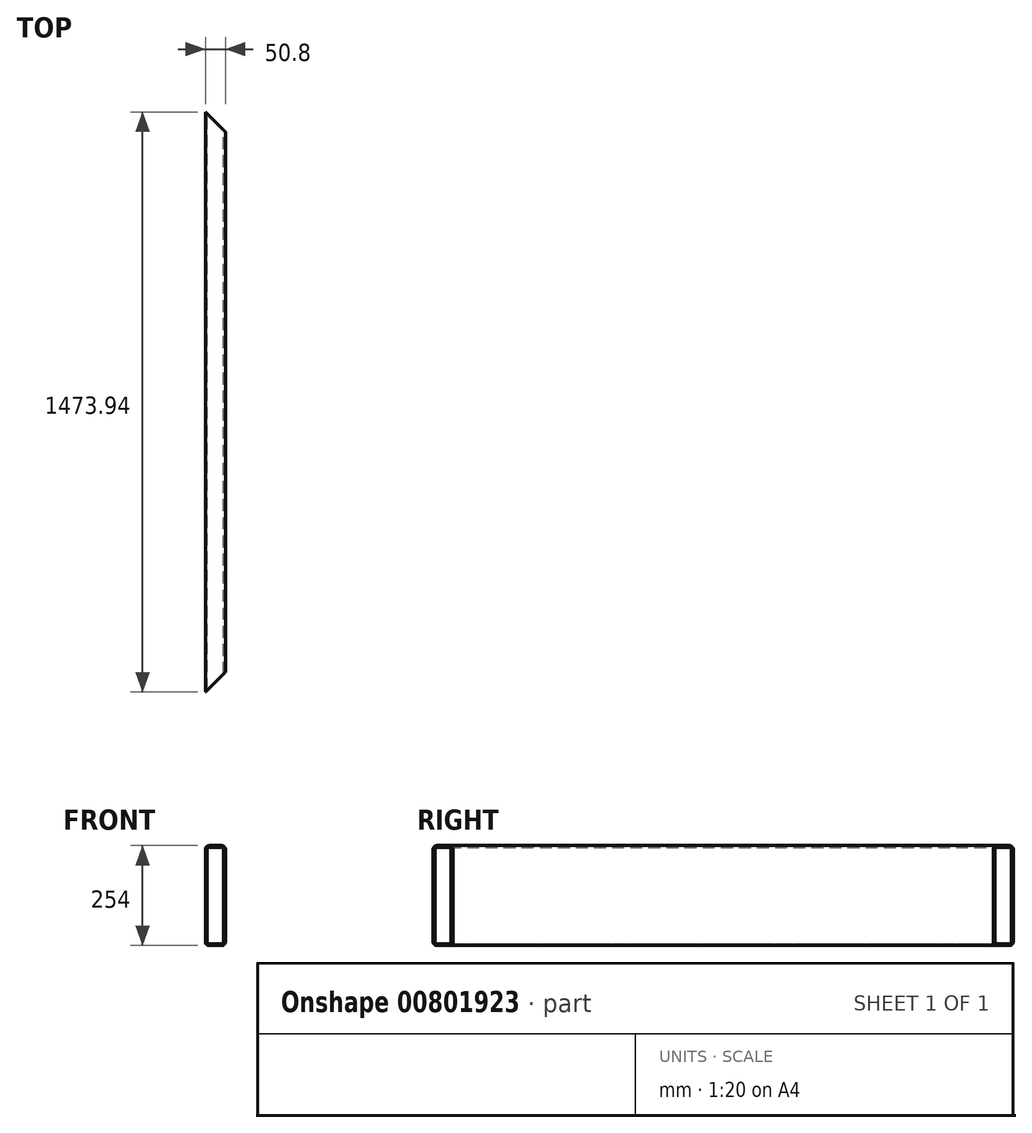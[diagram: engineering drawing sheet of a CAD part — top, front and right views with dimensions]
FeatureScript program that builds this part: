
annotation { "Feature Type Name" : "Feature", "Feature Type Description" : "" }
export const myFeature = defineFeature(function(context is Context, id is Id, definition is map)
    precondition{}
    {
        {
            var Q0;
            Q0=qCreatedBy(makeId("Front.planeOp"),FACE);
            var sketch = newSketch(context, id + "F0", { "sketchPlane" : qUnion([Q0])});
            skLineSegment(sketch, "E0.bottom", {"start": v(-9.52, 0) * mm, "end": v(-41.28, 0) * mm});
            skLineSegment(sketch, "E0.top", {"start": v(-9.53, 254) * mm, "end": v(-41.28, 254) * mm});
            skLineSegment(sketch, "E0.left", {"start": v(0, 9.53) * mm, "end": v(0, 244.47) * mm});
            skLineSegment(sketch, "E0.right", {"start": v(-50.8, 9.52) * mm, "end": v(-50.8, 244.47) * mm});
            skLineSegment(sketch, "E1.bottom", {"start": v(-41.3, 249.25) * mm, "end": v(-9.5, 249.25) * mm});
            skLineSegment(sketch, "E1.top", {"start": v(-41.3, 4.75) * mm, "end": v(-9.5, 4.75) * mm});
            skLineSegment(sketch, "E1.left", {"start": v(-46.05, 244.5) * mm, "end": v(-46.05, 9.5) * mm});
            skLineSegment(sketch, "E1.right", {"start": v(-4.75, 244.5) * mm, "end": v(-4.75, 9.5) * mm});
            skPoint(sketch, "E2.visualSharp", {"position": v(-46.05, 249.25) * mm});
            skArc(sketch, "E2.filletArc", {"start": v(-41.3, 249.25) * mm, "mid": v(-44.66, 247.86) * mm, "end": v(-46.05, 244.5) * mm});
            skPoint(sketch, "E3.visualSharp", {"position": v(-4.75, 249.25) * mm});
            skArc(sketch, "E3.filletArc", {"start": v(-4.75, 244.5) * mm, "mid": v(-6.14, 247.86) * mm, "end": v(-9.5, 249.25) * mm});
            skPoint(sketch, "E4.visualSharp", {"position": v(-4.75, 4.75) * mm});
            skArc(sketch, "E4.filletArc", {"start": v(-9.5, 4.75) * mm, "mid": v(-6.14, 6.14) * mm, "end": v(-4.75, 9.5) * mm});
            skPoint(sketch, "E5.visualSharp", {"position": v(-46.05, 4.75) * mm});
            skArc(sketch, "E5.filletArc", {"start": v(-46.05, 9.5) * mm, "mid": v(-44.66, 6.14) * mm, "end": v(-41.3, 4.75) * mm});
            skPoint(sketch, "E6.visualSharp", {"position": v(-50.8, 254) * mm});
            skArc(sketch, "E6.filletArc", {"start": v(-41.28, 254) * mm, "mid": v(-48.01, 251.21) * mm, "end": v(-50.8, 244.47) * mm});
            skPoint(sketch, "E7.visualSharp", {"position": v(0, 254) * mm});
            skArc(sketch, "E7.filletArc", {"start": v(0, 244.47) * mm, "mid": v(-2.79, 251.21) * mm, "end": v(-9.53, 254) * mm});
            skPoint(sketch, "E8.visualSharp", {"position": v(0, 0) * mm});
            skArc(sketch, "E8.filletArc", {"start": v(-9.52, 0) * mm, "mid": v(-2.79, 2.79) * mm, "end": v(0, 9.53) * mm});
            skPoint(sketch, "E9.visualSharp", {"position": v(-50.8, 0) * mm});
            skArc(sketch, "E9.filletArc", {"start": v(-50.8, 9.52) * mm, "mid": v(-48.01, 2.79) * mm, "end": v(-41.28, 0) * mm});
            skSolve(sketch);
        }
        {
            var Q0;
            Q0=qSketchRegion(id+"F0",true);
            extrude(context, id + "F1", {"entities" : qUnion([Q0]), "depth" : 1473.94 * mm});
        }
        {
            var Q0;
            Q0=makeQuery(id+"F1.opExtrude","SWEPT_FACE",FACE,{"disambiguationData":[OSD([sQuery(id+"F0.wireOp",EDGE,"E0.top")])]});
            var sketch = newSketch(context, id + "F2", { "sketchPlane" : qUnion([Q0])});
            skLineSegment(sketch, "E10", {"start": v(-50.8, -1473.94) * mm, "end": v(0, -1423.14) * mm});
            skLineSegment(sketch, "E11", {"start": v(0, -1423.14) * mm, "end": v(0, -1473.94) * mm});
            skLineSegment(sketch, "E12", {"start": v(0, -1473.94) * mm, "end": v(-50.8, -1473.94) * mm});
            skLineSegment(sketch, "E13", {"start": v(-50.8, 0) * mm, "end": v(0, -50.8) * mm});
            skLineSegment(sketch, "E14", {"start": v(0, -50.8) * mm, "end": v(0, 0) * mm});
            skLineSegment(sketch, "E15", {"start": v(0, 0) * mm, "end": v(-50.8, 0) * mm});
            skSolve(sketch);
        }
        {
            var Q0;
            Q0=qSketchRegion(id+"F2",true);
            extrude(context, id + "F3", {"entities" : qUnion([Q0]), "operationType" : NewBodyOperationType.REMOVE, "endBound" : BoundingType.THROUGH_ALL, "oppositeDirection" : true, "depth" : 25.4 * mm});
        }
        {
            var Q0;
            Q0=makeQuery(id+"F1.opExtrude","SWEPT_FACE",FACE,{"disambiguationData":[OSD([sQuery(id+"F0.wireOp",EDGE,"E0.left")])]});
            var sketch = newSketch(context, id + "F4", { "sketchPlane" : qUnion([Q0])});
            skLineSegment(sketch, "E16", {"start": v(-271.44, 383.12) * mm, "end": v(-298.41, 358.62) * mm});
            skLineSegment(sketch, "E17", {"start": v(-262.9, 386.42) * mm, "end": v(-220.1, 386.42) * mm});
            skLineSegment(sketch, "E18", {"start": v(-207.4, 373.72) * mm, "end": v(-207.4, 239) * mm});
            skLineSegment(sketch, "E19", {"start": v(-220.1, 226.3) * mm, "end": v(-289.88, 226.3) * mm});
            skLineSegment(sketch, "E20", {"start": v(-302.58, 239) * mm, "end": v(-302.58, 349.21) * mm});
            skArc(sketch, "E21.filletArc", {"start": v(-262.9, 386.42) * mm, "mid": v(-267.48, 385.56) * mm, "end": v(-271.44, 383.12) * mm});
            skPoint(sketch, "E22.visualSharp", {"position": v(-302.58, 354.84) * mm});
            skArc(sketch, "E22.filletArc", {"start": v(-298.41, 358.62) * mm, "mid": v(-301.49, 354.35) * mm, "end": v(-302.58, 349.21) * mm});
            skPoint(sketch, "E23.visualSharp", {"position": v(-302.58, 226.3) * mm});
            skArc(sketch, "E23.filletArc", {"start": v(-302.58, 239) * mm, "mid": v(-298.86, 230.01) * mm, "end": v(-289.88, 226.3) * mm});
            skPoint(sketch, "E24.visualSharp", {"position": v(-207.4, 226.3) * mm});
            skArc(sketch, "E24.filletArc", {"start": v(-220.1, 226.3) * mm, "mid": v(-211.12, 230.01) * mm, "end": v(-207.4, 239) * mm});
            skPoint(sketch, "E25.visualSharp", {"position": v(-207.4, 386.42) * mm});
            skArc(sketch, "E25.filletArc", {"start": v(-207.4, 373.72) * mm, "mid": v(-211.12, 382.7) * mm, "end": v(-220.1, 386.42) * mm});
            skSolve(sketch);
        }
        {
            var Q0;
            Q0=qSketchRegion(id+"F4",true);
            extrude(context, id + "F5", {"entities" : qUnion([Q0]), "depth" : 6.35 * mm, "offsetDistance" : 25 * mm});
        }
        {
            var Q0;
            Q0=makeQuery(id+"F5.opExtrude","SWEPT_BODY",BODY,{"disambiguationData":[OSD([sQuery(id+"F4.wireOp",EDGE,"E16"),sQuery(id+"F4.wireOp",EDGE,"E17"),sQuery(id+"F4.wireOp",EDGE,"E18"),sQuery(id+"F4.wireOp",EDGE,"E19"),sQuery(id+"F4.wireOp",EDGE,"E20"),sQuery(id+"F4.wireOp",EDGE,"E21.filletArc"),sQuery(id+"F4.wireOp",EDGE,"E22.filletArc"),sQuery(id+"F4.wireOp",EDGE,"E23.filletArc"),sQuery(id+"F4.wireOp",EDGE,"E24.filletArc"),sQuery(id+"F4.wireOp",EDGE,"E25.filletArc")])]});
            transform(context, id + "F6", {"entities" : qUnion([Q0]), "transformType" : TransformType.TRANSLATION_3D, "dx" : 0 * mm, "dy" : 0 * mm, "dz" : 0 * mm, "makeCopy" : true});
        }
        {
            var Q0;
            Q0=makeQuery(id+"F6.opPattern","COPY",BODY,{"derivedFrom":makeQuery(id+"F5.opExtrude","SWEPT_BODY",BODY,{"disambiguationData":[OSD([sQuery(id+"F4.wireOp",EDGE,"E16"),sQuery(id+"F4.wireOp",EDGE,"E17"),sQuery(id+"F4.wireOp",EDGE,"E18"),sQuery(id+"F4.wireOp",EDGE,"E19"),sQuery(id+"F4.wireOp",EDGE,"E20"),sQuery(id+"F4.wireOp",EDGE,"E21.filletArc"),sQuery(id+"F4.wireOp",EDGE,"E22.filletArc"),sQuery(id+"F4.wireOp",EDGE,"E23.filletArc"),sQuery(id+"F4.wireOp",EDGE,"E24.filletArc"),sQuery(id+"F4.wireOp",EDGE,"E25.filletArc")])]}),"instanceName":"1"});
            deleteBodies(context, id + "F7", {"entities" : qUnion([Q0])});
        }
        {
            var Q0;
            Q0=makeQuery(id+"F5.opExtrude","SWEPT_BODY",BODY,{"disambiguationData":[OSD([sQuery(id+"F4.wireOp",EDGE,"E16"),sQuery(id+"F4.wireOp",EDGE,"E17"),sQuery(id+"F4.wireOp",EDGE,"E18"),sQuery(id+"F4.wireOp",EDGE,"E19"),sQuery(id+"F4.wireOp",EDGE,"E20"),sQuery(id+"F4.wireOp",EDGE,"E21.filletArc"),sQuery(id+"F4.wireOp",EDGE,"E22.filletArc"),sQuery(id+"F4.wireOp",EDGE,"E23.filletArc"),sQuery(id+"F4.wireOp",EDGE,"E24.filletArc"),sQuery(id+"F4.wireOp",EDGE,"E25.filletArc")])]});
            deleteBodies(context, id + "F8", {"entities" : qUnion([Q0])});
        }
    });
